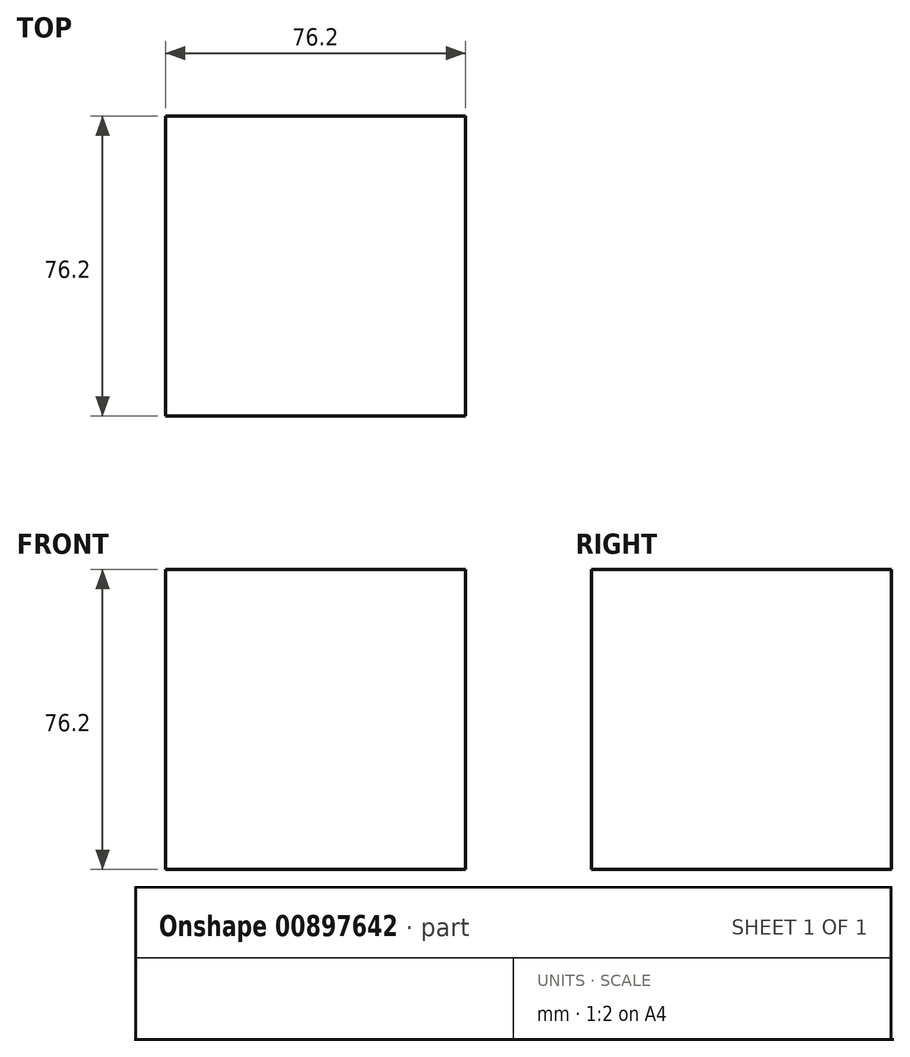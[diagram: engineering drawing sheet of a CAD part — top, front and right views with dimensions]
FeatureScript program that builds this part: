
annotation { "Feature Type Name" : "Feature", "Feature Type Description" : "" }
export const myFeature = defineFeature(function(context is Context, id is Id, definition is map)
    precondition{}
    {
        {
            var Q0;
            Q0=qCreatedBy(makeId("Front.planeOp"),FACE);
            var sketch = newSketch(context, id + "F0", { "sketchPlane" : qUnion([Q0])});
            skLineSegment(sketch, "E0.bottom", {"start": v(38.1, 38.1) * mm, "end": v(-38.1, 38.1) * mm});
            skLineSegment(sketch, "E0.top", {"start": v(38.1, -38.1) * mm, "end": v(-38.1, -38.1) * mm});
            skLineSegment(sketch, "E0.left", {"start": v(38.1, 38.1) * mm, "end": v(38.1, -38.1) * mm});
            skLineSegment(sketch, "E0.right", {"start": v(-38.1, 38.1) * mm, "end": v(-38.1, -38.1) * mm});
            skPoint(sketch, "E0.middle", {"position": v(0, 0) * mm});
            skSolve(sketch);
        }
        {
            var Q0;
            Q0=makeQuery(id+"F0.imprint","IMPRINT",FACE,{"disambiguationData":[TD([[makeQuery(id+"F0.imprint","IMPRINT",EDGE,{"derivedFrom":sQuery(id+"F0.wireOp",EDGE,"E0.bottom")}),1.0]])]});
            extrude(context, id + "F1", {"entities" : qUnion([Q0]), "depth" : 76.2 * mm, "offsetDistance" : 25.4 * mm});
        }
    });
